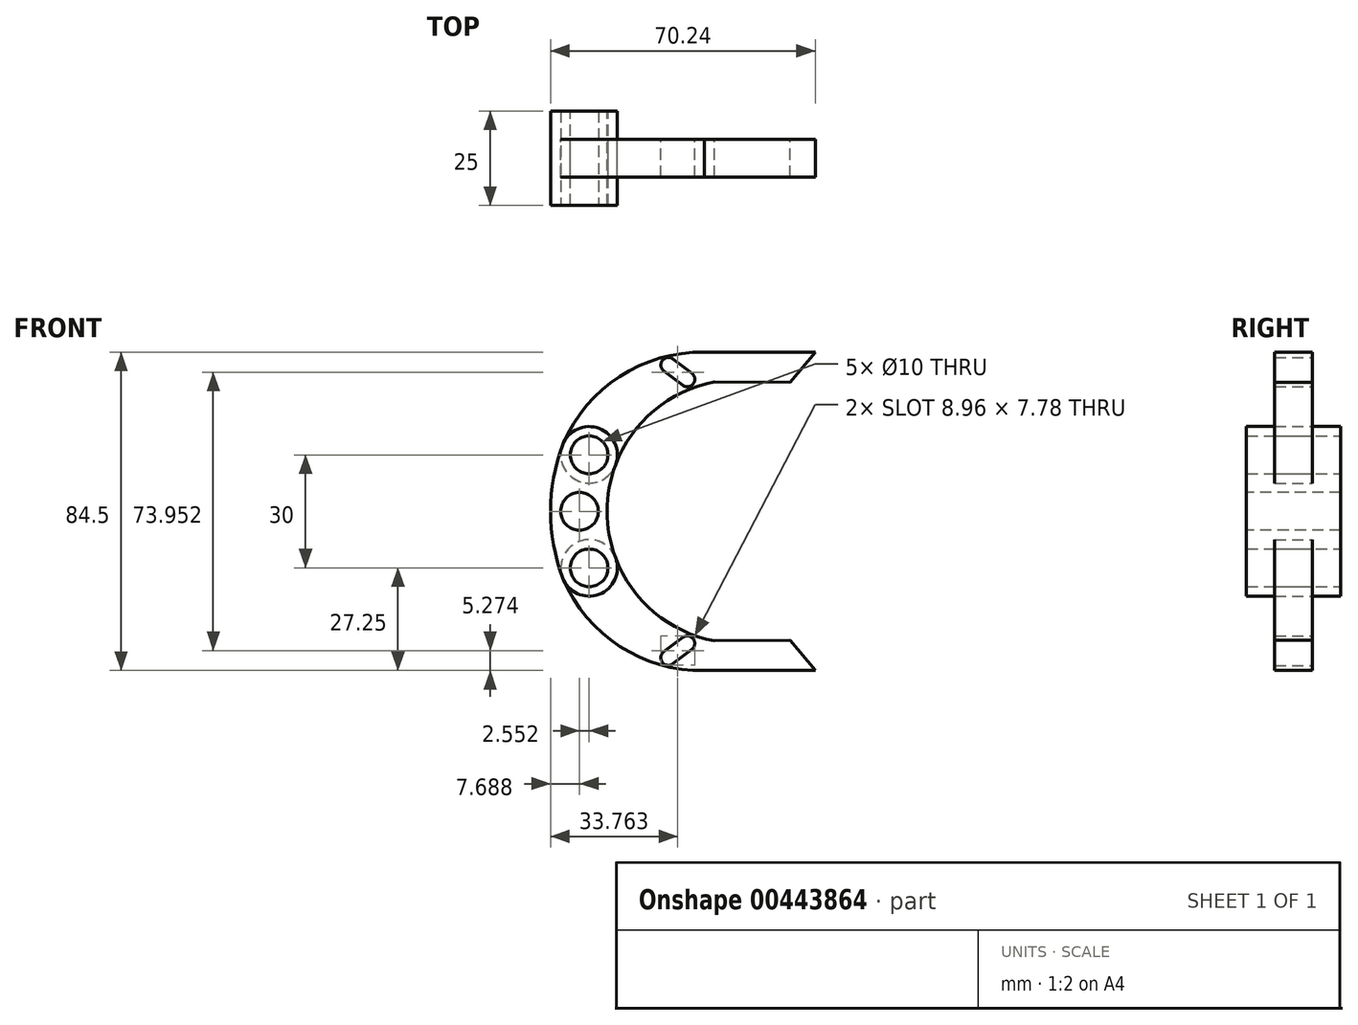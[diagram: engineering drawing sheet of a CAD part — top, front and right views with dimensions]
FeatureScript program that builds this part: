
annotation { "Feature Type Name" : "Feature", "Feature Type Description" : "" }
export const myFeature = defineFeature(function(context is Context, id is Id, definition is map)
    precondition{}
    {
        {
            var Q0;
            Q0=qCreatedBy(makeId("Front.planeOp"),FACE);
            var sketch = newSketch(context, id + "F0", { "sketchPlane" : qUnion([Q0])});
            skLineSegment(sketch, "E0", {"start": v(0, 15) * mm, "end": v(0, -15) * mm, "construction": true});
            skLineSegment(sketch, "E1", {"start": v(0, 0) * mm, "end": v(80.65, 0) * mm, "construction": true});
            skCircle(sketch, "E2", {"center": v(0, 15) * mm, "radius": 5 * mm});
            skCircle(sketch, "E3", {"center": v(0, -15) * mm, "radius": 5 * mm});
            skArc(sketch, "E4", {"start": v(-7.02, 17.65) * mm, "mid": v(-10.24, 0) * mm, "end": v(-7.02, -17.65) * mm});
            skArc(sketch, "E5", {"start": v(7.02, 12.35) * mm, "mid": v(4.76, 0) * mm, "end": v(7.02, -12.35) * mm});
            skArc(sketch, "E6.0", {"start": v(7.02, 12.35) * mm, "mid": v(2.65, 22.02) * mm, "end": v(-7.02, 17.65) * mm});
            skArc(sketch, "E7.0", {"start": v(-7.02, -17.65) * mm, "mid": v(2.65, -22.02) * mm, "end": v(7.02, -12.35) * mm});
            skSolve(sketch);
        }
        {
            var Q0;
            Q0=qCreatedBy(makeId("Front.planeOp"),FACE);
            var sketch = newSketch(context, id + "F1", { "sketchPlane" : qUnion([Q0])});
            skArc(sketch, "E8", {"start": v(30.57, 42.25) * mm, "mid": v(8.13, 35.81) * mm, "end": v(-6.9, 17.94) * mm});
            skArc(sketch, "E9", {"start": v(33.29, 34.4) * mm, "mid": v(17.27, 26.81) * mm, "end": v(7.02, 12.35) * mm});
            skLineSegment(sketch, "E10", {"start": v(30.57, 42.25) * mm, "end": v(60, 42.25) * mm});
            skLineSegment(sketch, "E11", {"start": v(60, 42.25) * mm, "end": v(53.29, 34.25) * mm});
            skLineSegment(sketch, "E12", {"start": v(53.29, 34.25) * mm, "end": v(33.29, 34.4) * mm});
            skCircle(sketch, "E13", {"center": v(0, 15) * mm, "radius": 7.5 * mm});
            skCircle(sketch, "E14.0.0", {"center": v(0, 15) * mm, "radius": 5 * mm});
            skPoint(sketch, "E15.orphan", {"position": v(-8.02, 15) * mm});
            skArc(sketch, "E16", {"start": v(22.24, 40.47) * mm, "mid": v(19.43, 40.1) * mm, "end": v(19.8, 37.3) * mm});
            skArc(sketch, "E17", {"start": v(24.8, 33.48) * mm, "mid": v(27.66, 33.92) * mm, "end": v(27.1, 36.76) * mm});
            skLineSegment(sketch, "E18", {"start": v(22.24, 40.47) * mm, "end": v(27.24, 36.66) * mm});
            skLineSegment(sketch, "E19", {"start": v(19.8, 37.3) * mm, "end": v(24.8, 33.48) * mm});
            skLineSegment(sketch, "E20", {"start": v(21.02, 38.88) * mm, "end": v(26.02, 35.07) * mm, "construction": true});
            skLineSegment(sketch, "E21", {"start": v(26.02, 35.07) * mm, "end": v(30.57, 42.25) * mm, "construction": true});
            skPoint(sketch, "E22.orphan", {"position": v(26.02, 32.55) * mm});
            skLineSegment(sketch, "E23.MirrorCS", {"start": v(21.02, -38.88) * mm, "end": v(26.02, -35.07) * mm, "construction": true});
            skArc(sketch, "E24.MirrorCS", {"start": v(24.8, -33.48) * mm, "mid": v(27.66, -33.92) * mm, "end": v(27.1, -36.76) * mm});
            skLineSegment(sketch, "E25.MirrorCS", {"start": v(26.02, -35.07) * mm, "end": v(30.57, -42.25) * mm, "construction": true});
            skPoint(sketch, "E26.MirrorP", {"position": v(-8.02, -15) * mm});
            skLineSegment(sketch, "E27.MirrorCS", {"start": v(19.8, -37.3) * mm, "end": v(24.8, -33.48) * mm});
            skLineSegment(sketch, "E28.MirrorCS", {"start": v(22.24, -40.47) * mm, "end": v(27.24, -36.66) * mm});
            skArc(sketch, "E29.MirrorCS", {"start": v(22.24, -40.47) * mm, "mid": v(19.43, -40.1) * mm, "end": v(19.8, -37.3) * mm});
            skCircle(sketch, "E30.MirrorC", {"center": v(0, -15) * mm, "radius": 5 * mm});
            skCircle(sketch, "E31.MirrorC", {"center": v(0, -15) * mm, "radius": 7.5 * mm});
            skLineSegment(sketch, "E32.MirrorCS", {"start": v(53.29, -34.25) * mm, "end": v(33.29, -34.4) * mm});
            skLineSegment(sketch, "E33.MirrorCS", {"start": v(60, -42.25) * mm, "end": v(53.29, -34.25) * mm});
            skLineSegment(sketch, "E34.MirrorCS", {"start": v(30.57, -42.25) * mm, "end": v(60, -42.25) * mm});
            skArc(sketch, "E35.MirrorCS", {"start": v(33.29, -34.4) * mm, "mid": v(17.27, -26.81) * mm, "end": v(7.02, -12.35) * mm});
            skArc(sketch, "E36.MirrorCS", {"start": v(30.57, -42.25) * mm, "mid": v(8.13, -35.81) * mm, "end": v(-6.9, -17.94) * mm});
            skPoint(sketch, "E37.MirrorP", {"position": v(26.02, -32.55) * mm});
            skSolve(sketch);
        }
        {
            var Q0;
            Q0 = qSketchRegion(id + "F0", true);
            extrude(context, id + "F2", {"entities" : qUnion([Q0]), "endBound" : BoundingType.SYMMETRIC, "depth" : 25 * mm});
        }
        {
            var Q0;
            {var subQ1=sQuery(id+"F1.wireOp",EDGE,"E27.MirrorCS");Q0=makeQuery(id+"F1.imprint","IMPRINT",FACE,{"disambiguationData":[TD([[makeQuery(id+"F1.imprint","IMPRINT",EDGE,{"derivedFrom":subQ1}),1.0]])]});}
            var Q1;
            Q1 = qSketchRegion(id + "F1", true);
            extrude(context, id + "F3", {"entities" : qUnion([Q0, Q1]), "endBound" : BoundingType.SYMMETRIC, "depth" : 10 * mm});
        }
        {
            var Q0;
            Q0=makeQuery(id+"F2.opExtrude","CAP_FACE",FACE,{"disambiguationData":[OSD([sQuery(id+"F0.wireOp",EDGE,"E2"),sQuery(id+"F0.wireOp",EDGE,"E3"),sQuery(id+"F0.wireOp",EDGE,"E4"),sQuery(id+"F0.wireOp",EDGE,"E5"),sQuery(id+"F0.wireOp",EDGE,"E6.0"),sQuery(id+"F0.wireOp",EDGE,"E7.0")])],"isStart":false});
            var sketch = newSketch(context, id + "F4", { "sketchPlane" : qUnion([Q0])});
            skCircle(sketch, "E38", {"center": v(-2.55, 0) * mm, "radius": 5 * mm});
            skPoint(sketch, "E39.orphan", {"position": v(0, 15) * mm});
            skPoint(sketch, "E40.end.orphan", {"position": v(0, -15) * mm});
            skSolve(sketch);
        }
        {
            var Q0;
            Q0=makeQuery(id+"F4.imprint","IMPRINT",FACE,{"disambiguationData":[TD([[makeQuery(id+"F4.imprint","IMPRINT",EDGE,{"derivedFrom":sQuery(id+"F4.wireOp",EDGE,"E38")}),1.0]])]});
            extrude(context, id + "F5", {"entities" : qUnion([Q0]), "operationType" : NewBodyOperationType.REMOVE, "endBound" : BoundingType.THROUGH_ALL, "oppositeDirection" : true, "depth" : 25 * mm});
        }
    });
